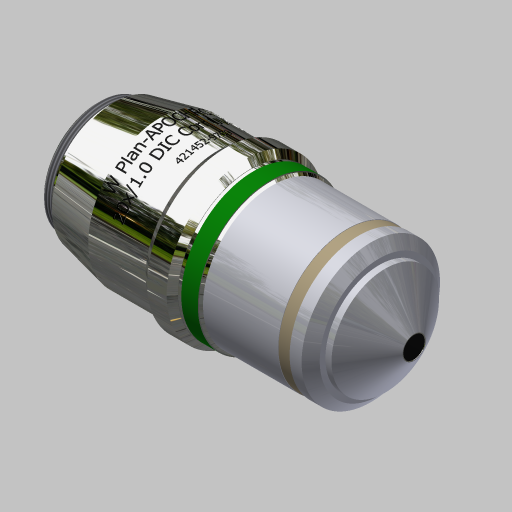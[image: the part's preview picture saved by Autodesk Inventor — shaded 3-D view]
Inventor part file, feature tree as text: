
AUTODESK INVENTOR PART (.ipt)
format: ipt  version: 2023 (Build 270158000, 158)  size: 5,491,712 bytes
history: native  units: mm
features: other x6, sketch x3, plane x2, hole x2, revolve x1, chamfer x1, thread x1
ambient origin geometry x8: Origin, YZ Plane, XZ Plane, XY Plane, X Axis, Y Axis, Z Axis, Center Point
bodies: Volumenkörper3 (feature_tree)
feature tree (16):
  sketch  "Sketch1"  dims[d10=17.5mm d12=3.9mm d13=76.6mm d16=2.8mm]
  other  "Work Axis1"
  other  "Work Point1"
  other  "back focal plane"
  revolve  "Umdrehung3"
  chamfer  "Fase1"  Distance=3.9mm
  thread  "Gewinde3"  [1 undecoded]
  plane  "Arbeitsebene2"
  other  "Prägen1"
  hole  "Hole2"  [1 undecoded]
  hole  "Hole3"  [1 undecoded]
  plane  "Arbeitsebene3"
  other  "Prägen2"
  sketch  "Skizze2"  dims[d19=2.0mm d20=1.0mm]
  sketch  "Skizze3"  dims[d27=4.0mm d28=90.0deg d29=0.5mm d30=2.0mm d31=45.0deg d32=10.0mm d33=0.0mm d35=0.1mm d36=0.0mm d37=10.0mm d38=10.0mm d39=12.0mm d40=6.0mm d41=4.0mm d42=2.0mm d43=90.0deg d44=6.9mm d45=0.0mm d62=10.0mm d63=10.0mm d48=5.25mm d49=6.0mm d50=4.0mm d51=2.0mm d52=90.0deg d53=0.1mm d54=0.0mm d55=0.1mm d56=0.0mm d64=6.021386mm d66=11.3mm d67=13.5mm d68=0.5mm d69=3.9mm d95=19.0mm d118=6.981317mm d122=64.2mm d129=0.1mm d135=16.75mm d136=56.5mm d137=59.3mm d138=0.1mm]
  other  "Image1"
note: 3 required parameter values undecoded (feature->parameter linkage not recoverable at this tier; creation-order binding heuristic only, values carry confidence <= 0.55)
